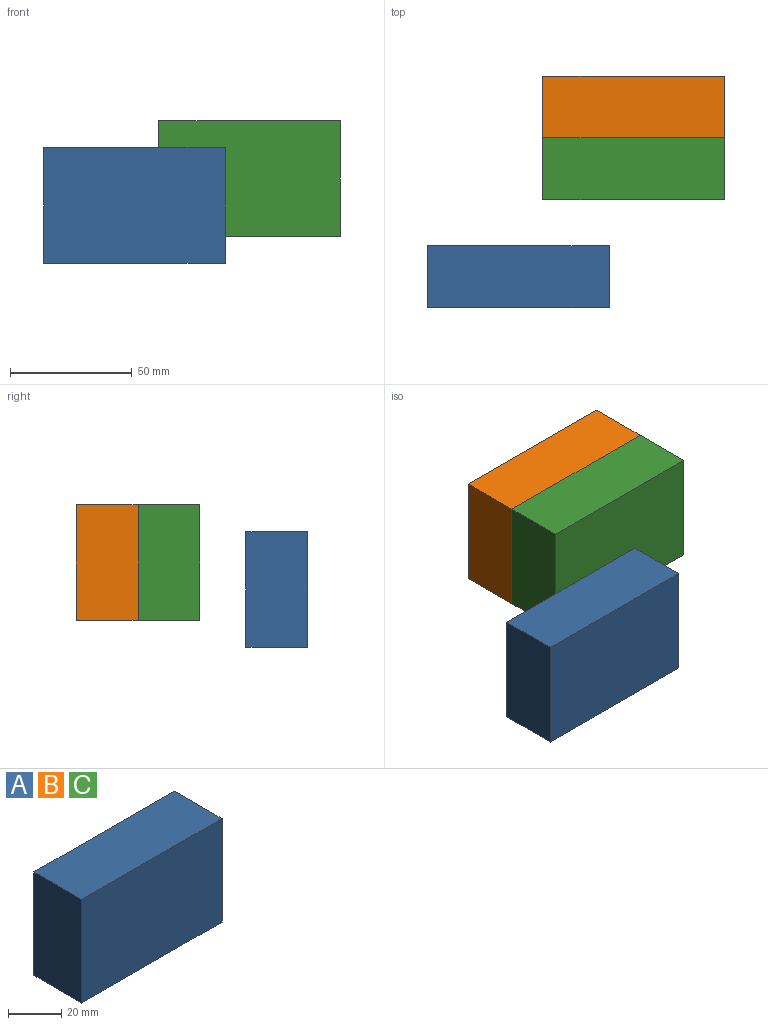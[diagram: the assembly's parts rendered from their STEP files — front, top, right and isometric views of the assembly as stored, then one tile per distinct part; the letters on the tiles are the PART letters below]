
ASSEMBLY  parts=3 mates=1
PART A: 6 faces, bbox 74.5x25.4x47.6 mm
  f0: plane 74.53x25.4mm, normal (0,0,1), area 1893.2mm2, adj f1,f3,f4,f5
  f1: plane 47.57x25.4mm, normal (-1,0,0), area 1208.3mm2, adj f0,f2,f4,f5
  f2: plane 74.53x25.4mm, normal (0,0,-1), area 1893.2mm2, adj f1,f3,f4,f5
  f3: plane 47.57x25.4mm, normal (1,0,0), area 1208.3mm2, adj f0,f2,f4,f5
  f4: plane 74.53x47.57mm, normal (0,-1,0), area 3545.8mm2, adj f0,f1,f2,f3
  f5: plane 74.53x47.57mm, normal (0,1,0), area 3545.8mm2, adj f0,f1,f2,f3
PART B: same geometry as A
PART C: same geometry as A
PLACE A rot(axis=(1,0,0),180deg) t=(-61.29,-151.11,31.26)mm
PLACE B t=(-13.94,-55.96,-13.76)mm
PLACE C rot(axis=(1,0,0),180deg) t=(-13.94,-106.76,42.36)mm
MATE parallel C.f4 <-> B.f4  axis (0,1,0) through (-135.44,-81.36,14.3)mm
